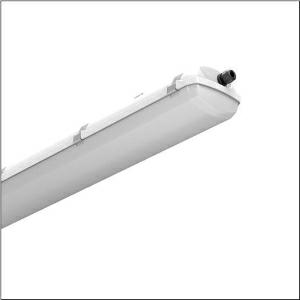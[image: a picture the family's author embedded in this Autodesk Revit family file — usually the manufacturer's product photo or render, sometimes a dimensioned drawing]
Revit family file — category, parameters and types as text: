
# Revit family: monsun_ex_51fxb27l480a
name_source: partatom
category: Lighting Fixtures
units: mm (PartAtom-declared; Revit-internal decimal feet)

## family parameters
Cut with Voids When Loaded = No
Host = Face
Light Source = No
Part Type = Normal
Room Calculation Point = No
Round Connector Dimension = Use Diameter
Shared = No

## types (1)
- Monsun Ex (1 x LED, 8720 lm, 58.4 W, 4000K)
    Apparent Load = 58 VA
    CIE Flux Codes = 43 72 91 92 100
    Color Rendering = 80
    Color Temperature = 4000K
    Default Elevation = 1800 mm
    Description = Monsun Ex, damp-proof luminaire, primary optical cover: cover, of PC, UV-stabilised, opal, light emission: direct distribution, primary light characteristic: symmetric, installation type: surface-mounted, LED, rated luminous flux: 8.720lm, luminous efficacy: 149lm/W, light colour: 840, colour temperature: 4000K, control gear: ON/OFF, with terminal, 3-pole, max. 2.5mm², through-wiring: 5x 2.5mm², mains connection: 220..240V, AC, 50/60Hz, rated input power: 58W, housing, of PC, light grey (RAL 7035), incl. blanking plug, incl. 2x Ex cable gland M20 for cable diameter 7..12mm with sealing, length: 1.280mm, width: 155mm, height: 105mm, clip for enclosure, of stainless steel, protection rating (complete): IP66, insulation class (complete): insulation class I (protective earthing), certification: CE, explosion class: zone2,22 II 3G Ex nR IIC T6 GC, II 3D Ex tc IIIC T80°C Dc, impact resistance: IK10, permissible operating ambient temperature: -20..+60°C, LABS conformity tested according to VDMA 24364:2018-05, contact your sales advisor before using the luminaires in applications with unclear chemical exposure, large temperature fluctuations or condensation-forming humidity, packaging unit: 1 piece
    Height = 105 mm
    Lamp = 1 x LED
    Lamp Light Flux = 8720 lm
    Lamp Power = 58.4 W
    Lamp count = 1
    Length = 1280 mm
    Luminous efficacy = 149 lm/W
    Manufacturer = Siteco
    ModVariant = No
    Model = 51FXB27L480A
    Mounting Place = Ceiling
    Mounting Type = Surface mounted
    Number of Poles = 1
    OnlyDefault = Yes
    Power Factor = 1
    Product Name = Monsun Ex
    Product group = damp-proof luminaire
    ProductGroupID = 300
    Protection Class = Protection class I
    Protection Degree = IP 66
    RLX_Detail_Level = 1
    RLX_Emergency_Light_Flux = 0 lm
    RLX_Emergency_Type = 0
    RLX_Emergency_Type_DB = No
    RlxData = <blob elided: 41637 chars, md5=fd325b0d>
    Socket = socket
    Standby Power = 0 W
    System Light Flux = 8720 lm
    System Power = 58 W
    Type Comments = Product without accessories
    Type Image = l_1258882.jpg
    URL = http://relux.com
    VarID = ---
    Voltage = 0 V
    Weight = 0.00 kg
    Width = 155 mm

## geometry (parser evidence)
native form markers: Blend x4, Sweep x13
no freeform markers — native parametric forms only
